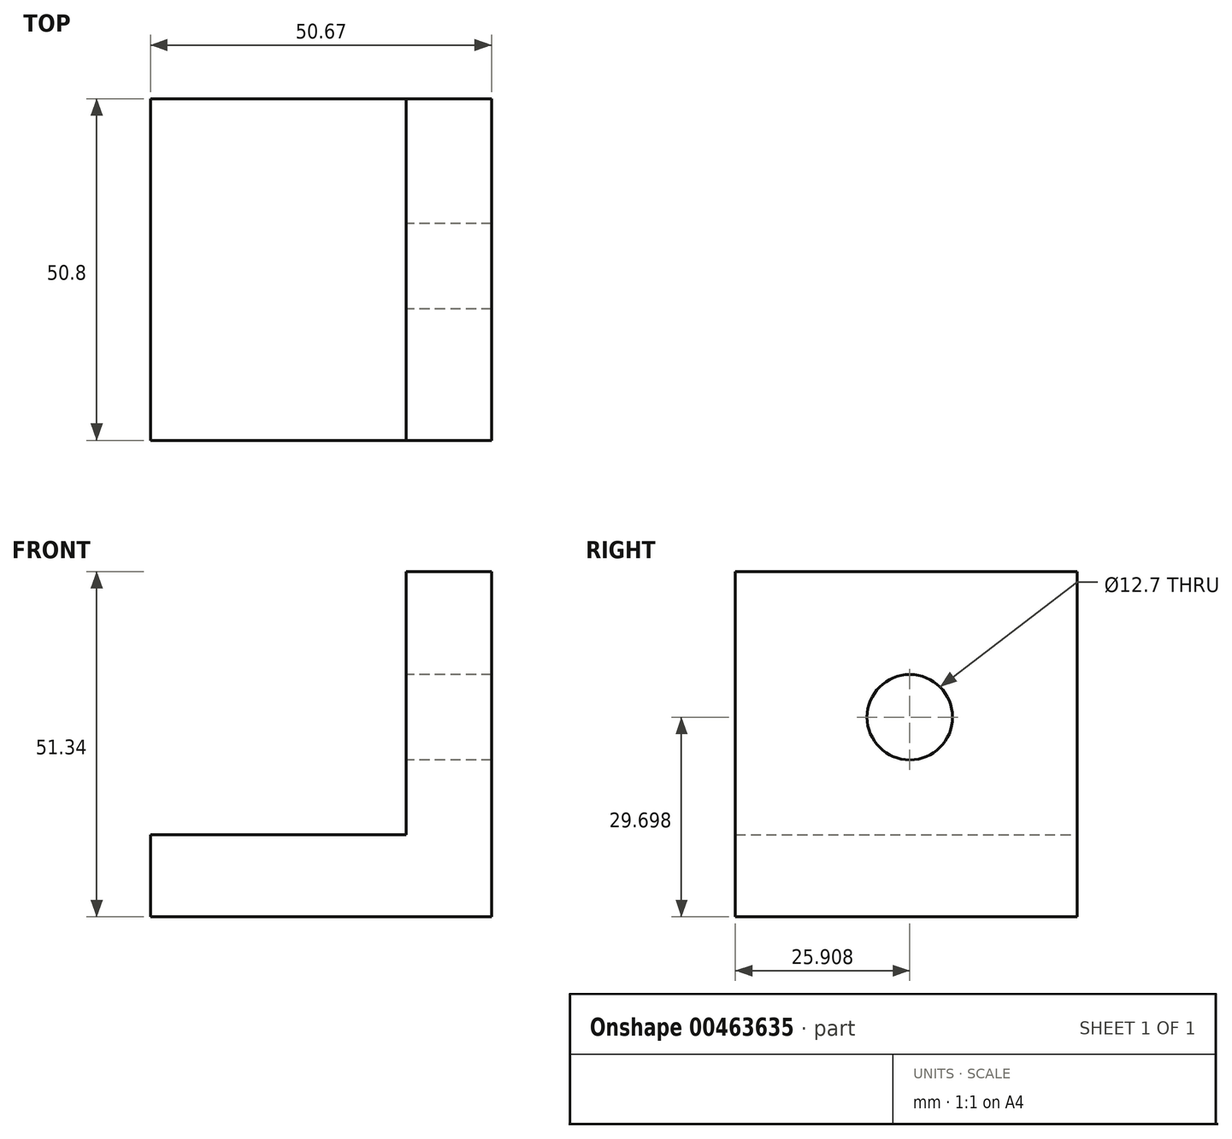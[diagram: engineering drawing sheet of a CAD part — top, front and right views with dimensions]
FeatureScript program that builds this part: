
annotation { "Feature Type Name" : "Feature", "Feature Type Description" : "" }
export const myFeature = defineFeature(function(context is Context, id is Id, definition is map)
    precondition{}
    {
        {
            var Q0;
            Q0=qCreatedBy(makeId("Front.planeOp"),FACE);
            var sketch = newSketch(context, id + "F0", { "sketchPlane" : qUnion([Q0])});
            skLineSegment(sketch, "E0.bottom", {"start": v(-20.9, 39.12) * mm, "end": v(29.78, 39.12) * mm});
            skLineSegment(sketch, "E0.top", {"start": v(-20.9, -12.22) * mm, "end": v(29.78, -12.22) * mm});
            skLineSegment(sketch, "E0.left", {"start": v(-20.9, 39.12) * mm, "end": v(-20.9, -12.22) * mm});
            skLineSegment(sketch, "E0.right", {"start": v(29.78, 39.12) * mm, "end": v(29.78, -12.22) * mm});
            skSolve(sketch);
        }
        {
            var Q0;
            Q0=makeQuery(id+"F0.imprint","IMPRINT",FACE,{"disambiguationData":[TD([[makeQuery(id+"F0.imprint","IMPRINT",EDGE,{"derivedFrom":sQuery(id+"F0.wireOp",EDGE,"E0.bottom")}),-1.0]])]});
            extrude(context, id + "F1", {"entities" : qUnion([Q0]), "depth" : 50.8 * mm});
        }
        {
            var Q0;
            Q0=makeQuery(id+"F1.opExtrude","CAP_FACE",FACE,{"disambiguationData":[OSD([sQuery(id+"F0.wireOp",EDGE,"E0.bottom"),sQuery(id+"F0.wireOp",EDGE,"E0.top"),sQuery(id+"F0.wireOp",EDGE,"E0.left"),sQuery(id+"F0.wireOp",EDGE,"E0.right")])],"isStart":true});
            var sketch = newSketch(context, id + "F2", { "sketchPlane" : qUnion([Q0])});
            skLineSegment(sketch, "E1.bottom", {"start": v(-29.78, 39.12) * mm, "end": v(-17.08, 39.12) * mm});
            skLineSegment(sketch, "E1.top", {"start": v(-29.78, -12.22) * mm, "end": v(-17.08, -12.22) * mm});
            skLineSegment(sketch, "E1.left", {"start": v(-29.78, 39.12) * mm, "end": v(-29.78, -12.22) * mm});
            skLineSegment(sketch, "E1.right", {"start": v(-17.08, 39.12) * mm, "end": v(-17.08, -12.22) * mm});
            skLineSegment(sketch, "E2.bottom", {"start": v(20.9, -12.22) * mm, "end": v(-29.78, -12.22) * mm});
            skLineSegment(sketch, "E2.top", {"start": v(20.9, 0) * mm, "end": v(-29.78, 0) * mm});
            skLineSegment(sketch, "E2.left", {"start": v(20.9, -12.22) * mm, "end": v(20.9, 0) * mm});
            skLineSegment(sketch, "E2.right", {"start": v(-29.78, -12.22) * mm, "end": v(-29.78, 0) * mm});
            skSolve(sketch);
        }
        {
            var Q0;
            Q0=makeQuery(id+"F1.opExtrude","SWEPT_FACE",FACE,{"disambiguationData":[OSD([sQuery(id+"F0.wireOp",EDGE,"E0.bottom")])]});
            var sketch = newSketch(context, id + "F3", { "sketchPlane" : qUnion([Q0])});
            skLineSegment(sketch, "E3", {"start": v(17.94, -50.8) * mm, "end": v(17.94, 0) * mm});
            skSolve(sketch);
        }
        {
            var Q0;
            {var subQ0=sQuery(id+"F2.wireOp",EDGE,"E1.right");var subQ3=sQuery(id+"F2.wireOp",EDGE,"E2.top");var subQ4=makeQuery(id+"F2.imprint","INTERSECT",VERTEX,{"derivedFrom":[subQ0,subQ3]});Q0=makeQuery(id+"F2.imprint","IMPRINT",FACE,{"disambiguationData":[TD([[makeQuery(id+"F2.imprint","IMPRINT",EDGE,{"disambiguationData":[TD([[subQ4,1.0]])],"derivedFrom":subQ0}),1.0]])]});}
            var sketch = newSketch(context, id + "F4", { "sketchPlane" : qUnion([Q0])});
            skSolve(sketch);
        }
        {
            var Q0;
            Q0 = qSketchRegion(id + "F4", true);
            var Q1;
            {var subQ0=sQuery(id+"F2.wireOp",EDGE,"E1.right");var subQ3=sQuery(id+"F2.wireOp",EDGE,"E2.top");var subQ4=makeQuery(id+"F2.imprint","INTERSECT",VERTEX,{"derivedFrom":[subQ0,subQ3]});Q1=makeQuery(id+"F2.imprint","IMPRINT",FACE,{"disambiguationData":[TD([[makeQuery(id+"F2.imprint","IMPRINT",EDGE,{"disambiguationData":[TD([[subQ4,1.0]])],"derivedFrom":subQ0}),1.0]])]});}
            extrude(context, id + "F5", {"entities" : qUnion([Q0, Q1]), "operationType" : NewBodyOperationType.REMOVE, "oppositeDirection" : true, "depth" : 25.4 * mm});
        }
        {
            var Q0;
            Q0=makeQuery(id+"F5.boolean.opBoolean","COPY",FACE,{"derivedFrom":makeQuery(id+"F5.opExtrude","CAP_FACE",FACE,{"disambiguationData":[OSD([sQuery(id+"F0.wireOp",EDGE,"E0.bottom"),sQuery(id+"F0.wireOp",EDGE,"E0.left"),sQuery(id+"F2.wireOp",EDGE,"E1.right"),sQuery(id+"F2.wireOp",EDGE,"E2.top")])],"isStart":false})});
            extrude(context, id + "F6", {"entities" : qUnion([Q0]), "operationType" : NewBodyOperationType.REMOVE, "oppositeDirection" : true, "depth" : 25.4 * mm});
        }
        {
            var Q0;
            {var subQ0=sQuery(id+"F2.wireOp",EDGE,"E1.right");Q0=makeQuery(id+"F6.boolean.opBoolean","MERGE",FACE,{"derivedFrom":[makeQuery(id+"F5.boolean.opBoolean","COPY",FACE,{"derivedFrom":makeQuery(id+"F5.opExtrude","SWEPT_FACE",FACE,{"disambiguationData":[OSD([subQ0])]})}),makeQuery(id+"F6.opExtrude","SWEPT_FACE",FACE,{"disambiguationData":[OSD([subQ0])]})]});}
            var sketch = newSketch(context, id + "F7", { "sketchPlane" : qUnion([Q0])});
            skCircle(sketch, "E4", {"center": v(24.9, 17.48) * mm, "radius": 6.35 * mm});
            skSolve(sketch);
        }
        {
            var Q0;
            Q0 = qSketchRegion(id + "F7", true);
            extrude(context, id + "F8", {"entities" : qUnion([Q0]), "operationType" : NewBodyOperationType.REMOVE, "oppositeDirection" : true, "depth" : 25.4 * mm});
        }
    });
